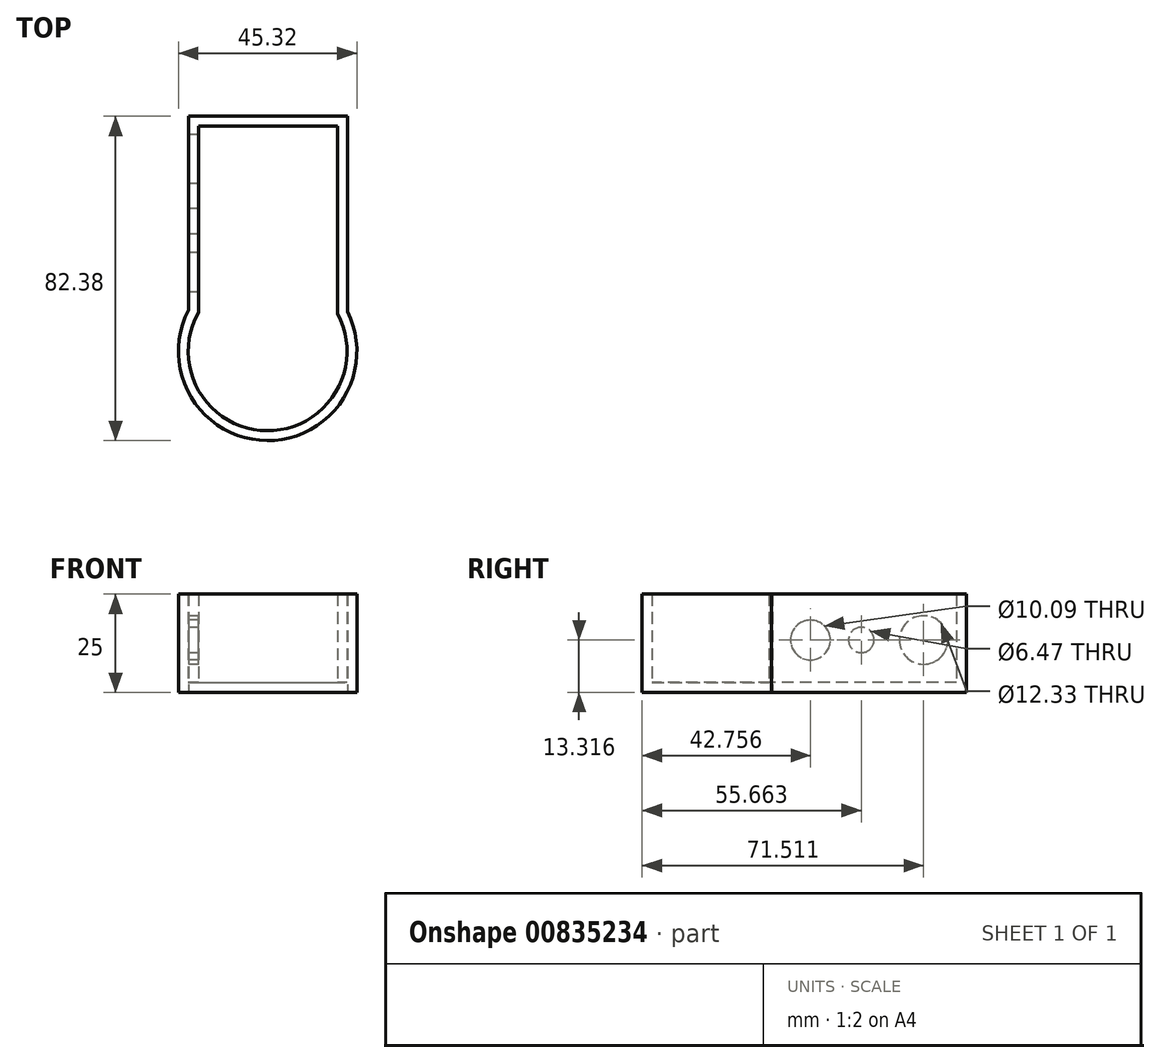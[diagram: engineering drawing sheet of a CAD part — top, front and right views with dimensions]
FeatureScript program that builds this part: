
annotation { "Feature Type Name" : "Feature", "Feature Type Description" : "" }
export const myFeature = defineFeature(function(context is Context, id is Id, definition is map)
    precondition{}
    {
        {
            var Q0;
            Q0=qCreatedBy(makeId("Top.planeOp"),FACE);
            var sketch = newSketch(context, id + "F0", { "sketchPlane" : qUnion([Q0])});
            skArc(sketch, "E0", {"start": v(-20.1, 10.48) * mm, "mid": v(-0.18, -22.66) * mm, "end": v(20.26, 10.16) * mm});
            skLineSegment(sketch, "E1.bottom", {"start": v(-20.1, 59.72) * mm, "end": v(20.26, 59.72) * mm});
            skLineSegment(sketch, "E1.left", {"start": v(-20.1, 59.72) * mm, "end": v(-20.1, 10.48) * mm});
            skLineSegment(sketch, "E1.right", {"start": v(20.26, 59.72) * mm, "end": v(20.26, 10.16) * mm});
            skSolve(sketch);
        }
        {
            var Q0;
            Q0=makeQuery(id+"F0.imprint","IMPRINT",FACE,{"disambiguationData":[TD([[makeQuery(id+"F0.imprint","IMPRINT",EDGE,{"derivedFrom":sQuery(id+"F0.wireOp",EDGE,"E0")}),1.0]])]});
            extrude(context, id + "F1", {"entities" : qUnion([Q0]), "depth" : 25 * mm, "offsetDistance" : 25 * mm});
        }
        {
            var Q0;
            Q0=makeQuery(id+"F1.opExtrude","CAP_FACE",FACE,{"disambiguationData":[OSD([sQuery(id+"F0.wireOp",EDGE,"E0"),sQuery(id+"F0.wireOp",EDGE,"E1.bottom"),sQuery(id+"F0.wireOp",EDGE,"E1.left"),sQuery(id+"F0.wireOp",EDGE,"E1.right")])],"isStart":false});
            shell(context, id + "F2", {"entities" : qUnion([Q0]), "thickness" : 2.5 * mm});
        }
        {
            var Q0;
            Q0=makeQuery(id+"F1.opExtrude","SWEPT_FACE",FACE,{"disambiguationData":[OSD([sQuery(id+"F0.wireOp",EDGE,"E1.left")])]});
            var sketch = newSketch(context, id + "F3", { "sketchPlane" : qUnion([Q0])});
            skCircle(sketch, "E2", {"center": v(-48.85, 13.32) * mm, "radius": 6.17 * mm});
            skCircle(sketch, "E3", {"center": v(-33, 13.32) * mm, "radius": 3.23 * mm});
            skCircle(sketch, "E4", {"center": v(-20.1, 13.32) * mm, "radius": 5.05 * mm});
            skSolve(sketch);
        }
        {
            var Q0;
            Q0 = qSketchRegion(id + "F3", true);
            extrude(context, id + "F4", {"entities" : qUnion([Q0]), "operationType" : NewBodyOperationType.REMOVE, "oppositeDirection" : true, "depth" : 25 * mm, "offsetDistance" : 25 * mm});
        }
    });
